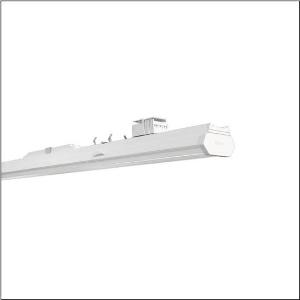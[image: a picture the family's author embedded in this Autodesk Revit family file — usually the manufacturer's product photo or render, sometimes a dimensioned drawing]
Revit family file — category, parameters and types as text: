
# Revit family: licross_r__21_protected_mo_52td11dn4a5g_03df
name_source: partatom
category: Lighting Fixtures
units: mm (PartAtom-declared; Revit-internal decimal feet)

## family parameters
Cut with Voids When Loaded = No
Host = Face
Light Source = No
Part Type = Normal
Room Calculation Point = No
Round Connector Dimension = Use Diameter
Shared = No

## types (1)
- --- (1 x LED, 10650 lm, 62 W, 4000K)
    Apparent Load = 62 VA
    CIE Flux Codes = 83 94 98 100 100
    Color Rendering = 80
    Color Temperature = 4000K
    Default Elevation = 1800 mm
    Description = Licross® 21 Protected MO, luminaire insert, of sheet steel, galvanised, coil coated, white, length: 1.500mm, width: 90mm, height: 103mm, LED rated luminous flux: 10.650lm, light colour: 840, control gear: DALI 2, with plug, 5-pole, with phase selection, mains connection: 220..240V, AC, 50/60Hz, rated input power: 62W, halogen-free wiring, primary light control with lens, of plastic, primary optical cover: cover, of PMMA, light emission: direct distribution, primary light characteristic: symmetric, protection rating (complete): IP54, insulation class (complete): insulation class I (protective earthing), certification: CE, ENEC, VDE, UKCA, protection symbol: D if used in an environment with non-conductive dust loads with corresponding accessories, impact resistance: IK06, permissible ambient temperature for indoor applications: -25..+35°C, corresponds to IFS (International Featured Standards) requirements for safety and quality in the food industry, reducing of maximum allowable ambient temperature of 5°C with ceiling mounting, LABS conformity tested according to VDMA 24364:2018-05, packaging unit: 1 piece
    Height = 92 mm
    Lamp = 1 x LED
    Lamp Light Flux = 10650 lm
    Lamp Power = 62 W
    Lamp count = 1
    Length = 1500 mm
    Luminous efficacy = 172 lm/W
    Manufacturer = Siteco
    ModVariant = No
    Model = 52TD11DN4A5G
    Mounting Place = Ceiling
    Mounting Type = Pendant
    Number of Poles = 1
    OnlyDefault = Yes
    Power Factor = 1
    Product Name = Licross® 21 Protected MO
    Product group = luminaire insert
    ProductGroupID = 901
    Protection Class = Protection class I
    Protection Degree = IP 54
    RLX_Detail_Level = 1
    RLX_Emergency_Light_Flux = 0 lm
    RLX_Emergency_Type = 0
    RLX_Emergency_Type_DB = No
    RlxData = <blob elided: 24173 chars, md5=13abf12e>
    Socket = socket
    Standby Power = 0 W
    System Light Flux = 10650 lm
    System Power = 62 W
    Type Comments = factory setting: luminous flux: 100 % | dim-lin: 254 | 418 mA
    Type Image = l_1256148.jpg
    URL = http://relux.com
    VarID = @adj_059911
    Voltage = 0 V
    Weight = 0.00 kg
    Width = 88 mm

## geometry (parser evidence)
native form markers: Blend x4, Sweep x11
no freeform markers — native parametric forms only
